# Revit family: HansWeitzel_52680
name_source: partatom
category: Allgemeines Modell
revit_build: Autodesk Revit 2017 (Build: 20160225_1515(x64)
units: mm (PartAtom-declared; Revit-internal decimal feet)

## family parameters
Arbeitsebenenbasiert = Nein
Beim Laden mit Abzugskörper schneiden = Nein
Bemaßung runder Anschluss = Durchmesser verwenden
Gemeinsam genutzt = Nein
Immer vertikal = Ja
Kann Basisbauteil für Bewehrung sein = Nein
Raumberechnungspunkt = Nein
Teiletyp = Normal

## types (1)
- HansWeitzel_52680
    BIM = https://media.live.bim.site
    BIMSITE_PRODUCT_ID = efd02a2e2b4f09da970f268e0a658b5af052e636
    Beschreibung = HZ-Sockelleiste SLF Plus Weiß, 2m mit zusätzl. Dichtlippe zum Boden
    Brandklasse B2 = Ja
    Breite [mm] = 2000
    Dekor = Plus Weiß
    Farbton = weiß
    GTIN = 4022023112412
    Gewicht unverpackt (netto) [kg] = 0.825
    HAN = 52680
    HeinzeBIM = https://www.heinze.de
    Hersteller = Hans Weitzel GmbH & Co. KG
    Höhe [mm] = 95
    Ist System = Nein
    Ist Zubehör = Nein
    Length3 = 400 mm  [stored 1.31234 ft]
    Menge pro Verpackungseinheit = 10
    Profilart = Sockelprofil
    Profilform = Hohlprofil
    Selbstverlöschend = Ja
    Tiefe (mm) = 39
    Typname = HZ-Sockelleiste SLF Plus Weiß, 2m
    Werkstoff = PVC
    max. Betriebstemperatur (°C) = 90

note: [stored X ft] marks values corroborated as IEEE doubles in the binary element streams (Revit-internal decimal feet)

## geometry (parser evidence)
native form markers: Sweep x2
no freeform markers — native parametric forms only
